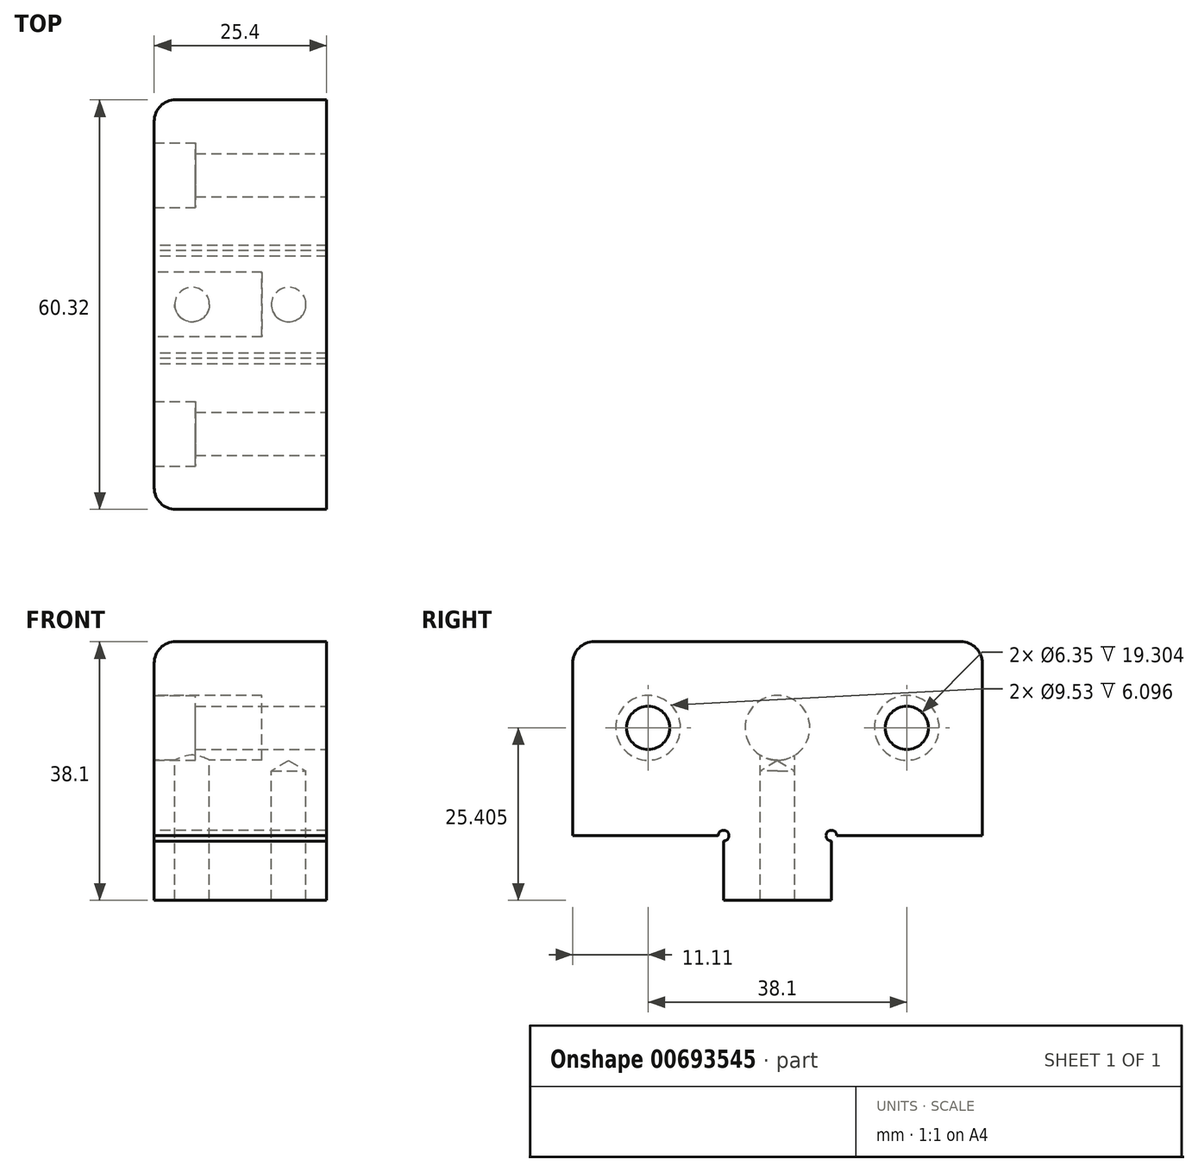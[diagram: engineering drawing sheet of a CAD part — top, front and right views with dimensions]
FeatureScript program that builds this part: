
annotation { "Feature Type Name" : "Feature", "Feature Type Description" : "" }
export const myFeature = defineFeature(function(context is Context, id is Id, definition is map)
    precondition{}
    {
        {
            var Q0;
            Q0=qCreatedBy(makeId("Right.planeOp"),FACE);
            var sketch = newSketch(context, id + "F0", { "sketchPlane" : qUnion([Q0])});
            skLineSegment(sketch, "E0", {"start": v(0, -9.53) * mm, "end": v(-7.94, -9.53) * mm});
            skLineSegment(sketch, "E1", {"start": v(-7.94, -9.53) * mm, "end": v(-7.94, -0.8) * mm});
            skLineSegment(sketch, "E2", {"start": v(-8.73, 0) * mm, "end": v(-30.16, 0) * mm});
            skLineSegment(sketch, "E3", {"start": v(-30.16, 0) * mm, "end": v(-30.16, 28.57) * mm});
            skLineSegment(sketch, "E4", {"start": v(-30.16, 28.57) * mm, "end": v(0, 28.57) * mm});
            skArc(sketch, "E5", {"start": v(-7.94, -0.8) * mm, "mid": v(-7.38, 0.56) * mm, "end": v(-8.73, 0) * mm});
            skLineSegment(sketch, "E6.MirrorCS", {"start": v(0, -9.52) * mm, "end": v(7.94, -9.52) * mm});
            skLineSegment(sketch, "E7.MirrorCS", {"start": v(7.94, -9.53) * mm, "end": v(7.94, -0.8) * mm});
            skArc(sketch, "E8.MirrorCS", {"start": v(7.94, -0.8) * mm, "mid": v(7.38, 0.56) * mm, "end": v(8.73, 0) * mm});
            skLineSegment(sketch, "E9.MirrorCS", {"start": v(8.73, 0) * mm, "end": v(30.16, 0) * mm});
            skLineSegment(sketch, "E10.MirrorCS", {"start": v(30.16, 28.58) * mm, "end": v(0, 28.58) * mm});
            skLineSegment(sketch, "E11.MirrorCS", {"start": v(30.16, 0) * mm, "end": v(30.16, 28.57) * mm});
            skCircle(sketch, "E12", {"center": v(0, 15.88) * mm, "radius": 4.76 * mm});
            skPoint(sketch, "E13", {"position": v(19.05, 15.88) * mm});
            skPoint(sketch, "E14.MirrorP", {"position": v(-19.05, 15.88) * mm});
            skSolve(sketch);
        }
        {
            var Q0;
            Q0=makeQuery(id+"F0.imprint","IMPRINT",FACE,{"disambiguationData":[TD([[makeQuery(id+"F0.imprint","IMPRINT",EDGE,{"derivedFrom":sQuery(id+"F0.wireOp",EDGE,"E0")}),-1.0]])]});
            var Q1;
            Q1=makeQuery(id+"F0.imprint","IMPRINT",FACE,{"disambiguationData":[TD([[makeQuery(id+"F0.imprint","IMPRINT",EDGE,{"derivedFrom":sQuery(id+"F0.wireOp",EDGE,"E12")}),1.0]])]});
            extrude(context, id + "F1", {"entities" : qUnion([Q0, Q1]), "depth" : 25.4 * mm, "offsetDistance" : 25.4 * mm});
        }
        {
            var Q0;
            Q0=sQuery(id+"F0.wireOp",VERTEX,"E14.MirrorP");
            var Q1;
            Q1=sQuery(id+"F0.wireOp",VERTEX,"E13");
            var Q2;
            Q2=makeQuery(id+"F1.opExtrude","SWEPT_BODY",BODY,{"disambiguationData":[OSD([sQuery(id+"F0.wireOp",EDGE,"E0"),sQuery(id+"F0.wireOp",EDGE,"E1"),sQuery(id+"F0.wireOp",EDGE,"E2"),sQuery(id+"F0.wireOp",EDGE,"E3"),sQuery(id+"F0.wireOp",EDGE,"E4"),sQuery(id+"F0.wireOp",EDGE,"E5"),sQuery(id+"F0.wireOp",EDGE,"E6.MirrorCS"),sQuery(id+"F0.wireOp",EDGE,"E7.MirrorCS"),sQuery(id+"F0.wireOp",EDGE,"E8.MirrorCS"),sQuery(id+"F0.wireOp",EDGE,"E9.MirrorCS"),sQuery(id+"F0.wireOp",EDGE,"E10.MirrorCS"),sQuery(id+"F0.wireOp",EDGE,"E11.MirrorCS")])]});
            hole(context, id + "F2", {"style" : HoleStyle.C_BORE, "endStyle" : HoleEndStyle.THROUGH, "oppositeDirection" : true, "holeDiameter" : 6.35 * mm, "cBoreDiameter" : 9.52 * mm, "cBoreDepth" : 6.1 * mm, "majorDiameter" : 6.35 * mm, "isTappedThrough" : true, "tappedDepth" : 7.14 * mm, "tapClearance" : 3, "locations" : qUnion([Q0, Q1]), "scope" : qUnion([Q2]), "startStyle" : HoleStartStyle.SKETCH});
        }
        {
            var Q0;
            Q0=makeQuery(id+"F0.imprint","IMPRINT",FACE,{"disambiguationData":[TD([[makeQuery(id+"F0.imprint","IMPRINT",EDGE,{"derivedFrom":sQuery(id+"F0.wireOp",EDGE,"E12")}),1.0]])]});
            extrude(context, id + "F3", {"entities" : qUnion([Q0]), "operationType" : NewBodyOperationType.REMOVE, "depth" : 15.88 * mm, "offsetDistance" : 25.4 * mm});
        }
        {
            var Q0;
            Q0=makeQuery(id+"F1.opExtrude","SWEPT_EDGE",EDGE,{"disambiguationData":[OSD([sQuery(id+"F0.wireOp",EDGE,"E3"),sQuery(id+"F0.wireOp",EDGE,"E4")])]});
            var Q1;
            Q1=makeQuery(id+"F1.opExtrude","SWEPT_EDGE",EDGE,{"disambiguationData":[OSD([sQuery(id+"F0.wireOp",EDGE,"E10.MirrorCS"),sQuery(id+"F0.wireOp",EDGE,"E11.MirrorCS")])]});
            var Q2;
            Q2=makeQuery(id+"F1.opExtrude","CAP_EDGE",EDGE,{"disambiguationData":[OSD([sQuery(id+"F0.wireOp",EDGE,"E4"),sQuery(id+"F0.wireOp",EDGE,"E10.MirrorCS")])],"isStart":true});
            var Q3;
            Q3=makeQuery(id+"F1.opExtrude","CAP_EDGE",EDGE,{"disambiguationData":[OSD([sQuery(id+"F0.wireOp",EDGE,"E3")])],"isStart":true});
            var Q4;
            Q4=makeQuery(id+"F1.opExtrude","CAP_EDGE",EDGE,{"disambiguationData":[OSD([sQuery(id+"F0.wireOp",EDGE,"E11.MirrorCS")])],"isStart":true});
            fillet(context, id + "F4", {"entities" : qUnion([Q0, Q1, Q2, Q3, Q4]), "radius" : 3.17 * mm, "tangentPropagation" : true, "allowEdgeOverflow" : false});
        }
        {
            var Q0;
            Q0=makeQuery(id+"F1.opExtrude","SWEPT_FACE",FACE,{"disambiguationData":[OSD([sQuery(id+"F0.wireOp",EDGE,"E0"),sQuery(id+"F0.wireOp",EDGE,"E6.MirrorCS")])]});
            var sketch = newSketch(context, id + "F5", { "sketchPlane" : qUnion([Q0])});
            skPoint(sketch, "E15", {"position": v(5.59, 0) * mm});
            skPoint(sketch, "E16", {"position": v(19.81, 0) * mm});
            skSolve(sketch);
        }
        {
            var Q0;
            Q0=sQuery(id+"F5.wireOp",VERTEX,"E15");
            var Q1;
            Q1=makeQuery(id+"F1.opExtrude","SWEPT_BODY",BODY,{"disambiguationData":[OSD([sQuery(id+"F0.wireOp",EDGE,"E0"),sQuery(id+"F0.wireOp",EDGE,"E1"),sQuery(id+"F0.wireOp",EDGE,"E2"),sQuery(id+"F0.wireOp",EDGE,"E3"),sQuery(id+"F0.wireOp",EDGE,"E4"),sQuery(id+"F0.wireOp",EDGE,"E5"),sQuery(id+"F0.wireOp",EDGE,"E6.MirrorCS"),sQuery(id+"F0.wireOp",EDGE,"E7.MirrorCS"),sQuery(id+"F0.wireOp",EDGE,"E8.MirrorCS"),sQuery(id+"F0.wireOp",EDGE,"E9.MirrorCS"),sQuery(id+"F0.wireOp",EDGE,"E10.MirrorCS"),sQuery(id+"F0.wireOp",EDGE,"E11.MirrorCS")])]});
            hole(context, id + "F6", {"style" : HoleStyle.SIMPLE, "endStyle" : HoleEndStyle.BLIND, "standardTappedOrClearance" : lookupTablePath({ "standard" : "ANSI", "engagement" : "75%", "pitch" : "20 tpi", "size" : "1/4", "type" : "Tapped" }), "standardBlindInLast" : lookupTablePath({ "standard" : "ANSI", "engagement" : "75%", "pitch" : "20 tpi", "size" : "1/4", "type" : "Tapped" }), "holeDiameter" : 5.1 * mm, "majorDiameter" : 6.35 * mm, "showTappedDepth" : true, "holeDepth" : 25.4 * mm, "isTappedThrough" : true, "tappedDepth" : 21.59 * mm, "tapClearance" : 3, "locations" : qUnion([Q0]), "scope" : qUnion([Q1]), "startStyle" : HoleStartStyle.SKETCH});
        }
        {
            var Q0;
            Q0=sQuery(id+"F5.wireOp",VERTEX,"E16");
            var Q1;
            Q1=makeQuery(id+"F1.opExtrude","SWEPT_BODY",BODY,{"disambiguationData":[OSD([sQuery(id+"F0.wireOp",EDGE,"E0"),sQuery(id+"F0.wireOp",EDGE,"E1"),sQuery(id+"F0.wireOp",EDGE,"E2"),sQuery(id+"F0.wireOp",EDGE,"E3"),sQuery(id+"F0.wireOp",EDGE,"E4"),sQuery(id+"F0.wireOp",EDGE,"E5"),sQuery(id+"F0.wireOp",EDGE,"E6.MirrorCS"),sQuery(id+"F0.wireOp",EDGE,"E7.MirrorCS"),sQuery(id+"F0.wireOp",EDGE,"E8.MirrorCS"),sQuery(id+"F0.wireOp",EDGE,"E9.MirrorCS"),sQuery(id+"F0.wireOp",EDGE,"E10.MirrorCS"),sQuery(id+"F0.wireOp",EDGE,"E11.MirrorCS")])]});
            hole(context, id + "F7", {"style" : HoleStyle.SIMPLE, "endStyle" : HoleEndStyle.BLIND, "standardTappedOrClearance" : lookupTablePath({ "standard" : "ANSI", "engagement" : "75%", "pitch" : "20 tpi", "size" : "1/4", "type" : "Tapped" }), "standardBlindInLast" : lookupTablePath({ "standard" : "ANSI", "engagement" : "75%", "pitch" : "20 tpi", "size" : "1/4", "type" : "Tapped" }), "holeDiameter" : 5.1 * mm, "majorDiameter" : 6.35 * mm, "showTappedDepth" : true, "holeDepth" : 19.05 * mm, "isTappedThrough" : true, "tappedDepth" : 15.24 * mm, "tapClearance" : 3, "locations" : qUnion([Q0]), "scope" : qUnion([Q1]), "startStyle" : HoleStartStyle.SKETCH});
        }
    });
